# Revit family: SH-5401
name_source: partatom
category: Lighting Fixtures
revit_build: Autodesk Revit 2017 (Build: 20160225_1515(x64)
units: mm (PartAtom-declared; Revit-internal decimal feet)

## family parameters
Cut with Voids When Loaded = No
Host = Face
Light Source = No
Part Type = Normal
Room Calculation Point = No
Round Connector Dimension = Use Diameter
Shared = No

## types (1)
- SH-5401(Gray color-4000K-LED)
    Body Material = Aluminum
    Body color = Gray color
    Default Elevation = 122 cm
    Diffuser = Diffuser
    Diffuser Material = polycarbonate
    Flicker = Low Flicker
    Height = 30 cm
    IP = IP54
    Lamp = LED
    Length = 8 cm
    Manufacturer = SHOA
    Model = SH-5401
    Protection Class = Class I
    Type medule = SMD-DOB
    URL = https://www.shoaco.com
    Voltage/Frequency = 230v/50hz
    Wattage. = 9 W
    Width = 16 cm
    color rendering index(CRI) = 80
    color temperature = 4000K
    consumption current = 0 A
    website = www.shoaco.com

## geometry (parser evidence)
native form markers: Blend x2, Sweep x5
no freeform markers — native parametric forms only
